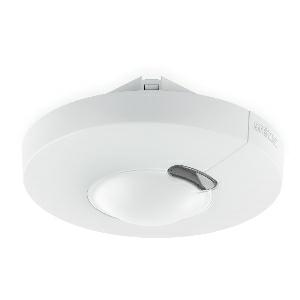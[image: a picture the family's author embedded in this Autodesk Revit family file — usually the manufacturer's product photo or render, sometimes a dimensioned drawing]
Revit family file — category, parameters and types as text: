
# Revit family: hf_3360_033682
name_source: partatom
category: Elektroinstallationen
revit_build: Autodesk Revit 2016 (Build: 20190508_0715(x64)
units: mm (PartAtom-declared; Revit-internal decimal feet)

## family parameters
Basisbauteil = Fläche
Beim Laden mit Abzugskörper schneiden = Nein
Bemaßung runder Anschluss = Durchmesser verwenden
Beschriftungsausrichtung beibehalten = Nein
Gemeinsam genutzt = Nein
Raumberechnungspunkt = Nein
Teiletyp = Normal

## types (1)
- HF 3360
    Apparent Load = 0 VA
    Beschreibung = Type: Motion detectors; Dimensions (Ø x H): 124 x 64 mm; Mains power supply: 220 – 240 V / 50 – 60 Hz; Sensor Technology: High frequency; Application, place: Indoors; Application, room: function room / ancillary room, stairwell, WC / washroom, multi-storey / underground car park, Indoors; Installation site: wall, ceiling, corner; Installation: Concealed wiring; HF-system: 5,8 GHz; Electronic scalability: Yes; Mechanical scalability: No; Mounting height: 2,00 – 4,00 m; Optimum mounting height: 2,8 m; Detection: also through glass, wood and stud walls; Detection angle: 360 °; Angle of aperture: 140 °; Sneak-by guard: Yes; Reach, radial: Ø 8 m (50 m²); Reach, tangential: Ø 8 m (50 m²); Twilight setting TEACH: Yes; Twilight setting: 2 – 1000 lx; Time setting: 5 sec – 15 min; Switching output 1, resistive: 2000 W; Switching output 1, number of LEDs / fluorescent lamps: 8 pcs.; Constant-lighting control: No; Basic light level function: No; Functions: Normal / test mode, Manual ON / ON-OFF; Settings via: Remote control, Potentiometers, Smart Remote; With remote control: Yes; Interconnection: Yes; IP-rating: IP20; Material: Plastic; Ambient temperature: -20 – 50 °C; Colour: white; Colour, RAL: 9003; Manufacturer's Warranty: 5 years; Version: COM1 - concealed, rd.; PU1, EAN: 4007841033682
    Height = 0 mm  [stored 0 ft]
    Hersteller = Steinel
    Length = 124 mm  [stored 0.406824 ft]
    ModVariant = Nein
    Modell = 033682
    Mounting Type = Recessed
    Number of Poles = 1
    OnlyDefault = Ja
    Power Factor = 1
    Product Name = HF 3360
    Product group = Sensor-switched indoor light
    ProductGroupID = 30
    Protection Class = Protection class
    Protection Degree = IP 20
    RlxData = <blob elided: 36489 chars, md5=c6424d6a>
    SensorDataFile = {"IESDataFiles":[]}
    Typenbild = produkt1_033682.jpg
    Typenkommentare = Product without accessories
    URL = http://relux.com
    VarID = ---
    Voltage = 0 V
    Vorgabe-Ansicht = 1800 mm
    Weight = 0.00 kg
    Width = 0 mm  [stored 0 ft]

note: [stored X ft] marks values corroborated as IEEE doubles in the binary element streams (Revit-internal decimal feet)

## geometry (parser evidence)
native form markers: Sweep x9
no freeform markers — native parametric forms only
